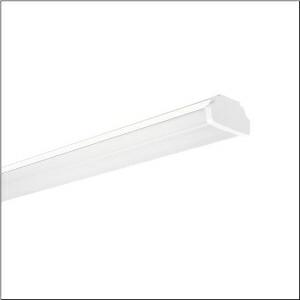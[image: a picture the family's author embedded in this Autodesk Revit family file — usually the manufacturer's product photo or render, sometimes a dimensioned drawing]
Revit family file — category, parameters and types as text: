
# Revit family: modario_r__31_ho_53bm812m1v4120_c9f3
name_source: partatom
category: Lighting Fixtures
units: mm (PartAtom-declared; Revit-internal decimal feet)

## family parameters
Cut with Voids When Loaded = No
Host = Face
Light Source = No
Part Type = Normal
Room Calculation Point = No
Round Connector Dimension = Use Diameter
Shared = No

## types (1)
- --- (1 x LED, 12380 lm, 77.3 W, 4000K)
    Apparent Load = 77 VA
    CIE Flux Codes = 47 80 95 92 100
    Color Rendering = 80
    Color Temperature = 4000K
    Default Elevation = 1800 mm
    Description = Modario® 31 HO, luminaire insert, of sheet steel, coil coated, white, length: 1.495mm, width: 81mm, height: 82mm, 5x system unit, system units: 299mm, LED rated luminous flux: 12.380lm, light colour: 840, control gear: ON/OFF Multilumen, control gear: ECG Multilumen, with plug, 3-pole, with phase selection, mains connection: 220..240V, AC, 50/60Hz, rated input power: 77W, through-wiring accessed according to module size, primary optical cover: cover, of PMMA, light emission: direct distribution, primary light characteristic: symmetric, protection rating (complete): IP20, protection rating (LED compartment): IP50, insulation class (complete): insulation class I (protective earthing), certification: CE, ENEC, VDE, UKCA, impact resistance: IK03, permissible ambient temperature for indoor applications: -35..+35°C, corresponds to IFS (International Featured Standards) requirements for safety and quality in the food industry, reducing of maximum allowable ambient temperature of 5°C with ceiling mounting, packaging unit: 1 piece
    Height = 92 mm
    Lamp = 1 x LED
    Lamp Light Flux = 12380 lm
    Lamp Power = 77.3 W
    Lamp count = 1
    Length = 1495 mm
    Luminous efficacy = 160 lm/W
    Manufacturer = Siteco
    ModVariant = No
    Model = 53BM812M1V4120
    Mounting Place = Ceiling
    Mounting Type = Pendant
    Number of Poles = 1
    OnlyDefault = Yes
    Power Factor = 1
    Product Name = Modario® 31 HO
    Product group = luminaire insert
    ProductGroupID = 902
    Protection Class = Protection class I
    Protection Degree = IP 20
    RLX_Detail_Level = 1
    RLX_Emergency_Light_Flux = 0 lm
    RLX_Emergency_Type = 0
    RLX_Emergency_Type_DB = No
    RlxData = <blob elided: 39969 chars, md5=68510a85>
    Socket = socket
    Standby Power = 0 W
    System Light Flux = 12380 lm
    System Power = 77 W
    Type Comments = factory setting: luminous flux: 100 % | (A | C | E) | 173 mA
    Type Image = l_1341886.jpg
    URL = http://relux.com
    VarID = @adj_199322
    Voltage = 0 V
    Weight = 0.00 kg
    Width = 81 mm

## geometry (parser evidence)
native form markers: Blend x4, Sweep x11
no freeform markers — native parametric forms only
